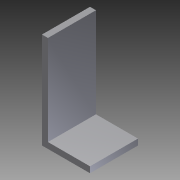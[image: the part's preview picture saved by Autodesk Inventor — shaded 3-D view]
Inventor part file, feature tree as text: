
AUTODESK INVENTOR PART (.ipt)
format: ipt  version: 2012 (Build 160160000, 160)  size: 72,192 bytes
history: native  units: in
note: dims shown in document units (in); Inventor stores cm internally (conversion verified against a paired STEP export)
features: extrude x1, sketch x1
ambient origin geometry x8: Origin, YZ Plane, XZ Plane, XY Plane, X Axis, Y Axis, Z Axis, Center Point
bodies: Solid1 (feature_tree)
feature tree (2):
  extrude  "Extrusion1"  Depth=1.0in
  sketch  "Sketch1"  dims[d0=2.0in d1=1.0in d2=0.1242in d3=1.0in d4=0.0in]
